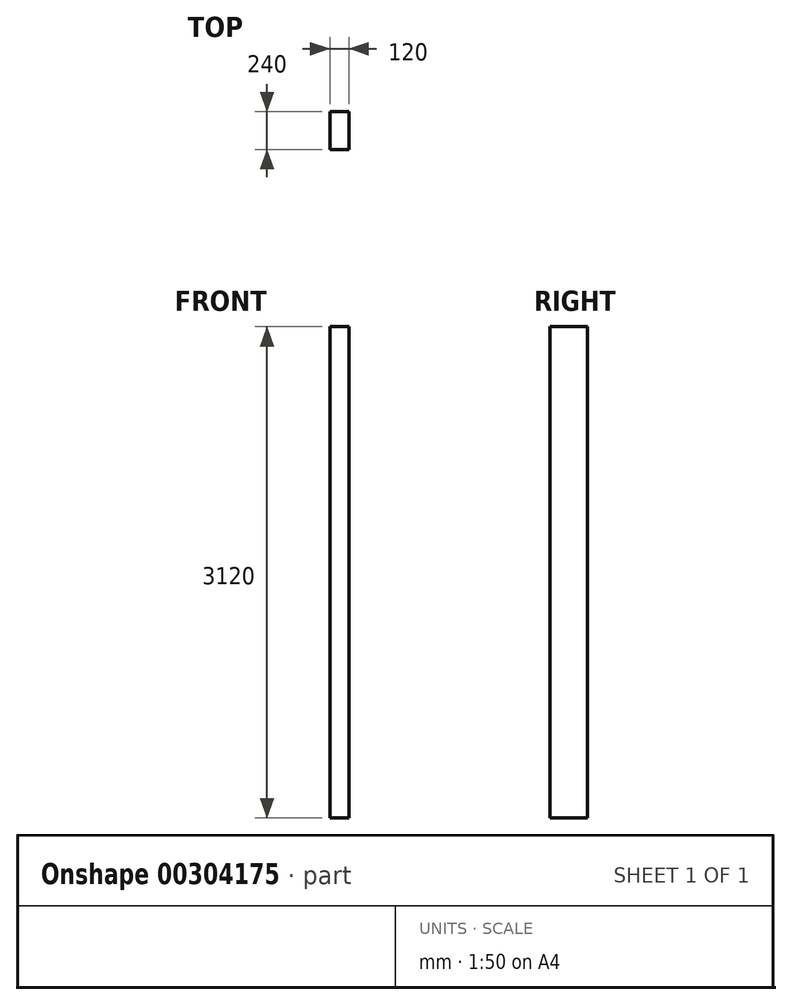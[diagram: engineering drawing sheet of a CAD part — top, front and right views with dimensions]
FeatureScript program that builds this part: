
annotation { "Feature Type Name" : "Feature", "Feature Type Description" : "" }
export const myFeature = defineFeature(function(context is Context, id is Id, definition is map)
    precondition{}
    {
        {
            var Q0;
            Q0=qCreatedBy(makeId("Top.planeOp"),FACE);
            var sketch = newSketch(context, id + "F0", { "sketchPlane" : qUnion([Q0])});
            skLineSegment(sketch, "E0.bottom", {"start": v(-65.23, 139.86) * mm, "end": v(54.77, 139.86) * mm});
            skLineSegment(sketch, "E0.top", {"start": v(-65.23, -100.14) * mm, "end": v(54.77, -100.14) * mm});
            skLineSegment(sketch, "E0.left", {"start": v(-65.23, 139.86) * mm, "end": v(-65.23, -100.14) * mm});
            skLineSegment(sketch, "E0.right", {"start": v(54.77, 139.86) * mm, "end": v(54.77, -100.14) * mm});
            skSolve(sketch);
        }
        {
            var Q0;
            Q0=makeQuery(id+"F0.imprint","IMPRINT",FACE,{"disambiguationData":[TD([[makeQuery(id+"F0.imprint","IMPRINT",EDGE,{"derivedFrom":sQuery(id+"F0.wireOp",EDGE,"E0.bottom")}),-1.0]])]});
            extrude(context, id + "F1", {"entities" : qUnion([Q0]), "depth" : 3120 * mm});
        }
    });
